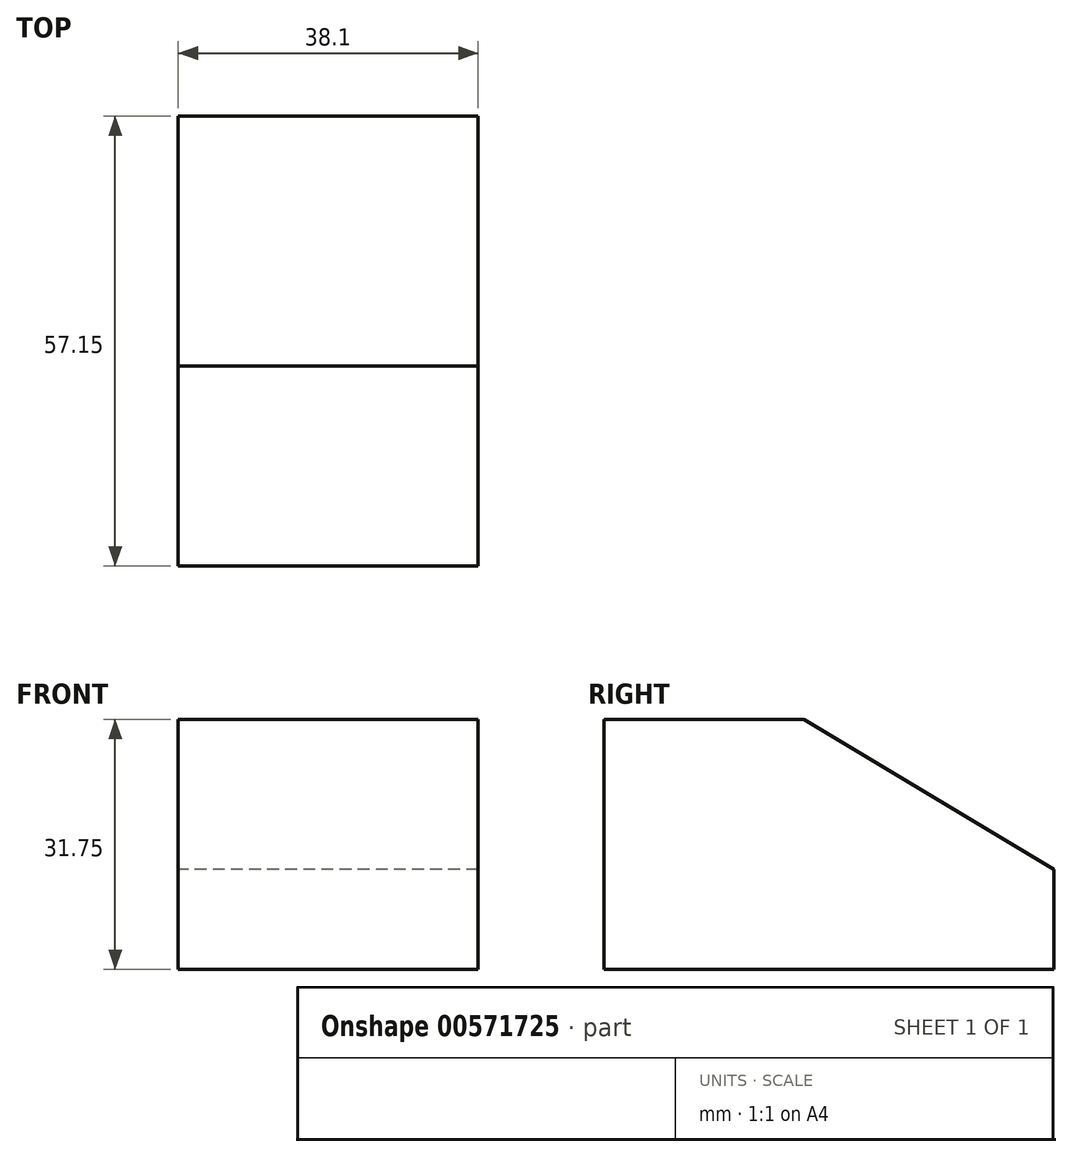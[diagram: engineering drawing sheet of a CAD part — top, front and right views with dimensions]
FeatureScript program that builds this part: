
annotation { "Feature Type Name" : "Feature", "Feature Type Description" : "" }
export const myFeature = defineFeature(function(context is Context, id is Id, definition is map)
    precondition{}
    {
        {
            var Q0;
            Q0=qCreatedBy(makeId("Right.planeOp"),FACE);
            var sketch = newSketch(context, id + "F0", { "sketchPlane" : qUnion([Q0])});
            skLineSegment(sketch, "E0", {"start": v(0, 0) * mm, "end": v(0, -31.75) * mm});
            skLineSegment(sketch, "E1", {"start": v(0, -31.75) * mm, "end": v(57.15, -31.75) * mm});
            skLineSegment(sketch, "E2", {"start": v(57.15, -31.75) * mm, "end": v(57.15, -19.05) * mm});
            skLineSegment(sketch, "E3", {"start": v(57.15, -19.05) * mm, "end": v(25.4, 0) * mm});
            skLineSegment(sketch, "E4", {"start": v(25.4, 0) * mm, "end": v(0, 0) * mm});
            skLineSegment(sketch, "E5", {"start": v(0, 0) * mm, "end": v(25.4, 0) * mm});
            skSolve(sketch);
        }
        {
            var Q0;
            Q0=makeQuery(id+"F0.imprint","IMPRINT",FACE,{"disambiguationData":[TD([[makeQuery(id+"F0.imprint","IMPRINT",EDGE,{"derivedFrom":sQuery(id+"F0.wireOp",EDGE,"E0")}),1.0]])]});
            extrude(context, id + "F1", {"entities" : qUnion([Q0]), "depth" : 25.4 * mm, "offsetDistance" : 25.4 * mm});
        }
        {
            var Q0;
            Q0=makeQuery(id+"F1.opExtrude","CAP_FACE",FACE,{"disambiguationData":[OSD([sQuery(id+"F0.wireOp",EDGE,"E0"),sQuery(id+"F0.wireOp",EDGE,"E1"),sQuery(id+"F0.wireOp",EDGE,"E2"),sQuery(id+"F0.wireOp",EDGE,"E3"),sQuery(id+"F0.wireOp",EDGE,"E5")])],"isStart":false});
            extrude(context, id + "F2", {"entities" : qUnion([Q0]), "operationType" : NewBodyOperationType.ADD, "depth" : 12.7 * mm, "offsetDistance" : 25.4 * mm});
        }
    });
